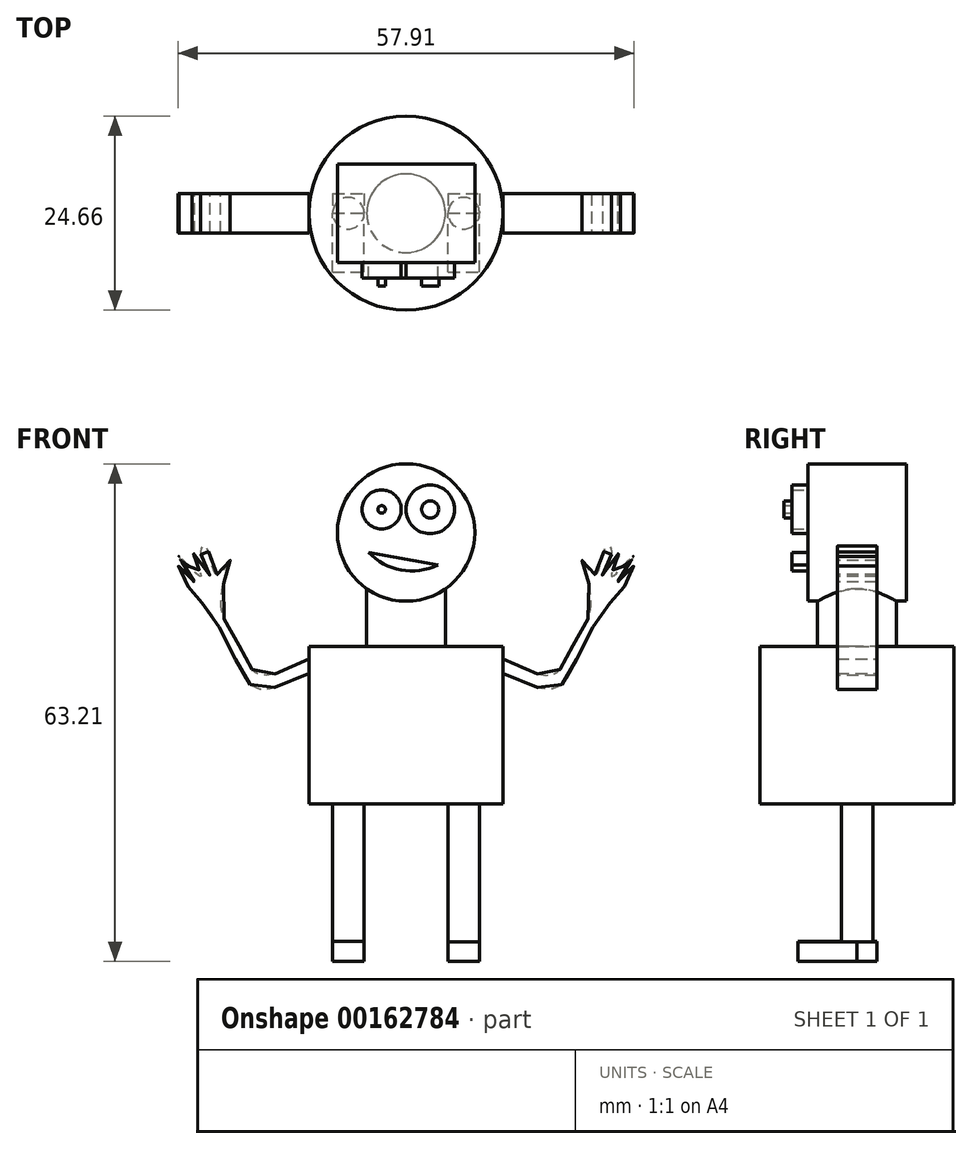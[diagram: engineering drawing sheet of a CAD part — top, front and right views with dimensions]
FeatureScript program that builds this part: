
annotation { "Feature Type Name" : "Feature", "Feature Type Description" : "" }
export const myFeature = defineFeature(function(context is Context, id is Id, definition is map)
    precondition{}
    {
        {
            var Q0;
            Q0=qCreatedBy(makeId("Top.planeOp"),FACE);
            var sketch = newSketch(context, id + "F0", { "sketchPlane" : qUnion([Q0])});
            skCircle(sketch, "E0", {"center": v(-14.66, 0) * mm, "radius": 4 * mm});
            skCircle(sketch, "E1", {"center": v(14.66, 0) * mm, "radius": 4 * mm});
            skSolve(sketch);
        }
        {
            var Q0;
            Q0 = qSketchRegion(id + "F0", true);
            extrude(context, id + "F1", {"entities" : qUnion([Q0]), "depth" : 35 * mm});
        }
        {
            var Q0;
            Q0=makeQuery(id+"F1.opExtrude","CAP_FACE",FACE,{"disambiguationData":[OSD([sQuery(id+"F0.wireOp",EDGE,"E0")])],"isStart":false});
            var sketch = newSketch(context, id + "F2", { "sketchPlane" : qUnion([Q0])});
            skCircle(sketch, "E2.0.0", {"center": v(-14.66, 0) * mm, "radius": 4 * mm});
            skCircle(sketch, "E3.0.0", {"center": v(14.66, 0) * mm, "radius": 4 * mm});
            skCircle(sketch, "E4", {"center": v(0, 0) * mm, "radius": 24.66 * mm});
            skSolve(sketch);
        }
        {
            var Q0;
            Q0=makeQuery(id+"F2.imprint","IMPRINT",FACE,{"disambiguationData":[TD([[makeQuery(id+"F2.imprint","IMPRINT",EDGE,{"derivedFrom":sQuery(id+"F2.wireOp",EDGE,"E2.0.0")}),-1.0]])]});
            var Q1;
            Q1=makeQuery(id+"F2.imprint","IMPRINT",FACE,{"disambiguationData":[TD([[makeQuery(id+"F2.imprint","IMPRINT",EDGE,{"derivedFrom":sQuery(id+"F2.wireOp",EDGE,"E2.0.0")}),1.0]])]});
            var Q2;
            Q2=makeQuery(id+"F2.imprint","IMPRINT",FACE,{"disambiguationData":[TD([[makeQuery(id+"F2.imprint","IMPRINT",EDGE,{"derivedFrom":sQuery(id+"F2.wireOp",EDGE,"E3.0.0")}),1.0]])]});
            extrude(context, id + "F3", {"entities" : qUnion([Q0, Q1, Q2]), "depth" : 40 * mm});
        }
        {
            var Q0;
            Q0=makeQuery(id+"F3.opExtrude","CAP_FACE",FACE,{"disambiguationData":[OSD([sQuery(id+"F2.wireOp",EDGE,"E4")])],"isStart":false});
            var sketch = newSketch(context, id + "F4", { "sketchPlane" : qUnion([Q0])});
            skCircle(sketch, "E5.0", {"center": v(0, 0) * mm, "radius": 24.66 * mm});
            skCircle(sketch, "E6", {"center": v(0, 0) * mm, "radius": 10 * mm});
            skSolve(sketch);
        }
        {
            var Q0;
            Q0=makeQuery(id+"F4.imprint","IMPRINT",FACE,{"disambiguationData":[TD([[makeQuery(id+"F4.imprint","IMPRINT",EDGE,{"derivedFrom":sQuery(id+"F4.wireOp",EDGE,"E6")}),1.0]])]});
            extrude(context, id + "F5", {"entities" : qUnion([Q0]), "operationType" : NewBodyOperationType.ADD, "depth" : 20 * mm});
        }
        {
            var Q0;
            Q0=qCreatedBy(makeId("Front.planeOp"),FACE);
            var sketch = newSketch(context, id + "F6", { "sketchPlane" : qUnion([Q0])});
            skLineSegment(sketch, "E7", {"start": v(-24.66, 35) * mm, "end": v(-24.66, 75) * mm});
            skFitSpline(sketch, "E8", {"points": [v(-24.66, 71.8) * mm, v(-37.62, 67.99) * mm, v(-42.3, 75.12) * mm, v(-47.07, 86.66) * mm, v(-44.74, 96.9) * mm, v(-48.05, 93.32) * mm, v(-50.89, 100.34) * mm, v(-52.23, 99.27) * mm, v(-49.9, 93.2) * mm, v(-54.41, 99.03) * mm, v(-52.18, 92.84) * mm, v(-57.71, 97.95) * mm, v(-53.74, 91.41) * mm, v(-57.72, 95.46) * mm, v(-55.3, 90.1) * mm, v(-51.17, 85.35) * mm, v(-43.7, 72.62) * mm, v(-38.04, 64.42) * mm, v(-24.66, 68.24) * mm], "startDerivative": vector(-210.68, -104.1) * mm, "endDerivative": vector(210.3, 100.49) * mm});
            skFitSpline(sketch, "E9.MirrorCS", {"points": [v(24.66, 71.8) * mm, v(37.62, 67.99) * mm, v(42.3, 75.12) * mm, v(47.07, 86.66) * mm, v(44.74, 96.9) * mm, v(48.05, 93.32) * mm, v(50.89, 100.34) * mm, v(52.23, 99.27) * mm, v(49.9, 93.2) * mm, v(54.41, 99.03) * mm, v(52.18, 92.84) * mm, v(57.71, 97.95) * mm, v(53.74, 91.41) * mm, v(57.72, 95.46) * mm, v(55.3, 90.1) * mm, v(51.17, 85.35) * mm, v(43.7, 72.62) * mm, v(38.04, 64.42) * mm, v(24.66, 68.24) * mm], "startDerivative": vector(210.68, -104.1) * mm, "endDerivative": vector(-210.3, 100.49) * mm});
            skLineSegment(sketch, "E10", {"start": v(24.66, 75) * mm, "end": v(24.66, 35) * mm});
            skSolve(sketch);
        }
        {
            var Q0;
            {var subQ0=sQuery(id+"F6.wireOp",EDGE,"E8");Q0=makeQuery(id+"F6.imprint","IMPRINT",FACE,{"disambiguationData":[TD([[makeQuery(id+"F6.imprint","IMPRINT",EDGE,{"derivedFrom":subQ0}),1.0]])]});}
            var Q1;
            {var subQ0=sQuery(id+"F6.wireOp",EDGE,"E9.MirrorCS");Q1=makeQuery(id+"F6.imprint","IMPRINT",FACE,{"disambiguationData":[TD([[makeQuery(id+"F6.imprint","IMPRINT",EDGE,{"derivedFrom":subQ0}),-1.0]])]});}
            extrude(context, id + "F7", {"entities" : qUnion([Q0, Q1]), "endBound" : BoundingType.SYMMETRIC, "depth" : 10 * mm});
        }
        {
            var Q0;
            Q0=qCreatedBy(makeId("Front.planeOp"),FACE);
            var sketch = newSketch(context, id + "F8", { "sketchPlane" : qUnion([Q0])});
            skLineSegment(sketch, "E11", {"start": v(10, 95) * mm, "end": v(10, 75) * mm});
            skLineSegment(sketch, "E12", {"start": v(-10, 75) * mm, "end": v(-10, 95) * mm});
            skCircle(sketch, "E13", {"center": v(0, 104) * mm, "radius": 17.45 * mm});
            skSolve(sketch);
        }
        {
            var Q0;
            Q0 = qSketchRegion(id + "F8", true);
            extrude(context, id + "F9", {"entities" : qUnion([Q0]), "operationType" : NewBodyOperationType.ADD, "endBound" : BoundingType.SYMMETRIC, "depth" : 25 * mm});
        }
        {
            var Q0;
            Q0=qCreatedBy(makeId("Front.planeOp"),FACE);
            var sketch = newSketch(context, id + "F10", { "sketchPlane" : qUnion([Q0])});
            skLineSegment(sketch, "E14", {"start": v(-18.66, 0.09) * mm, "end": v(-18.66, 35) * mm});
            skLineSegment(sketch, "E15", {"start": v(-10.66, 35) * mm, "end": v(-10.66, 0.09) * mm});
            skLineSegment(sketch, "E16", {"start": v(10.66, 0.04) * mm, "end": v(10.66, 35) * mm});
            skLineSegment(sketch, "E17", {"start": v(18.66, 35) * mm, "end": v(18.66, 0.04) * mm});
            skLineSegment(sketch, "E18.bottom", {"start": v(-18.66, 0.09) * mm, "end": v(-10.66, 0.09) * mm});
            skLineSegment(sketch, "E18.top", {"start": v(-18.66, -4.91) * mm, "end": v(-10.66, -4.91) * mm});
            skLineSegment(sketch, "E18.left", {"start": v(-18.66, 0.09) * mm, "end": v(-18.66, -4.91) * mm});
            skLineSegment(sketch, "E18.right", {"start": v(-10.66, 0.09) * mm, "end": v(-10.66, -4.91) * mm});
            skLineSegment(sketch, "E19.bottom", {"start": v(10.66, 0.04) * mm, "end": v(18.66, 0.04) * mm});
            skLineSegment(sketch, "E19.top", {"start": v(10.66, -4.96) * mm, "end": v(18.66, -4.96) * mm});
            skLineSegment(sketch, "E19.left", {"start": v(10.66, 0.04) * mm, "end": v(10.66, -4.96) * mm});
            skLineSegment(sketch, "E19.right", {"start": v(18.66, 0.04) * mm, "end": v(18.66, -4.96) * mm});
            skSolve(sketch);
        }
        {
            var Q0;
            Q0=makeQuery(id+"F10.imprint","IMPRINT",FACE,{"disambiguationData":[TD([[makeQuery(id+"F10.imprint","IMPRINT",EDGE,{"derivedFrom":sQuery(id+"F10.wireOp",EDGE,"E18.bottom")}),-1.0]])]});
            var Q1;
            Q1=makeQuery(id+"F10.imprint","IMPRINT",FACE,{"disambiguationData":[TD([[makeQuery(id+"F10.imprint","IMPRINT",EDGE,{"derivedFrom":sQuery(id+"F10.wireOp",EDGE,"E19.bottom")}),-1.0]])]});
            extrude(context, id + "F11", {"entities" : qUnion([Q0, Q1]), "depth" : 15 * mm});
        }
        {
            var Q0;
            Q0=makeQuery(id+"F11.opExtrude","CAP_FACE",FACE,{"disambiguationData":[OSD([sQuery(id+"F10.wireOp",EDGE,"E18.bottom"),sQuery(id+"F10.wireOp",EDGE,"E18.top"),sQuery(id+"F10.wireOp",EDGE,"E18.left"),sQuery(id+"F10.wireOp",EDGE,"E18.right")])],"isStart":true});
            var Q1;
            Q1=makeQuery(id+"F11.opExtrude","CAP_FACE",FACE,{"disambiguationData":[OSD([sQuery(id+"F10.wireOp",EDGE,"E19.bottom"),sQuery(id+"F10.wireOp",EDGE,"E19.top"),sQuery(id+"F10.wireOp",EDGE,"E19.left"),sQuery(id+"F10.wireOp",EDGE,"E19.right")])],"isStart":true});
            extrude(context, id + "F12", {"entities" : qUnion([Q0, Q1]), "depth" : 5 * mm});
        }
        {
            var Q0;
            Q0=makeQuery(id+"F7.opExtrude","SWEPT_BODY",BODY,{"disambiguationData":[OSD([sQuery(id+"F6.wireOp",EDGE,"E9.MirrorCS"),sQuery(id+"F6.wireOp",EDGE,"E10")])]});
            var Q1;
            Q1=makeQuery(id+"F7.opExtrude","SWEPT_BODY",BODY,{"disambiguationData":[OSD([sQuery(id+"F6.wireOp",EDGE,"E7"),sQuery(id+"F6.wireOp",EDGE,"E8")])]});
            var Q2;
            Q2=makeQuery(id+"F11.opExtrude","SWEPT_BODY",BODY,{"disambiguationData":[OSD([sQuery(id+"F10.wireOp",EDGE,"E18.bottom"),sQuery(id+"F10.wireOp",EDGE,"E18.top"),sQuery(id+"F10.wireOp",EDGE,"E18.left"),sQuery(id+"F10.wireOp",EDGE,"E18.right")])]});
            var Q3;
            Q3=makeQuery(id+"F3.opExtrude","SWEPT_BODY",BODY,{"disambiguationData":[OSD([sQuery(id+"F2.wireOp",EDGE,"E4")])]});
            var Q4;
            Q4=makeQuery(id+"F1.opExtrude","SWEPT_BODY",BODY,{"disambiguationData":[OSD([sQuery(id+"F0.wireOp",EDGE,"E1")])]});
            var Q5;
            Q5=makeQuery(id+"F11.opExtrude","SWEPT_BODY",BODY,{"disambiguationData":[OSD([sQuery(id+"F10.wireOp",EDGE,"E19.bottom"),sQuery(id+"F10.wireOp",EDGE,"E19.top"),sQuery(id+"F10.wireOp",EDGE,"E19.left"),sQuery(id+"F10.wireOp",EDGE,"E19.right")])]});
            var Q6;
            Q6=makeQuery(id+"F1.opExtrude","SWEPT_BODY",BODY,{"disambiguationData":[OSD([sQuery(id+"F0.wireOp",EDGE,"E0")])]});
            var Q7;
            Q7=makeQuery(id+"F12.opExtrude","SWEPT_BODY",BODY,{"disambiguationData":[OSD([sQuery(id+"F10.wireOp",EDGE,"E19.bottom"),sQuery(id+"F10.wireOp",EDGE,"E19.top"),sQuery(id+"F10.wireOp",EDGE,"E19.left"),sQuery(id+"F10.wireOp",EDGE,"E19.right")])]});
            var Q8;
            Q8=makeQuery(id+"F12.opExtrude","SWEPT_BODY",BODY,{"disambiguationData":[OSD([sQuery(id+"F10.wireOp",EDGE,"E18.bottom"),sQuery(id+"F10.wireOp",EDGE,"E18.top"),sQuery(id+"F10.wireOp",EDGE,"E18.left"),sQuery(id+"F10.wireOp",EDGE,"E18.right")])]});
            var Q9;
            Q9=makeQuery(id+"F11.opExtrude","CAP_VERTEX",VERTEX,{"disambiguationData":[OSD([sQuery(id+"F10.wireOp",EDGE,"E18.bottom"),sQuery(id+"F10.wireOp",EDGE,"E18.left")])],"isStart":false});
            transform(context, id + "F13", {"entities" : qUnion([Q0, Q1, Q2, Q3, Q4, Q5, Q6, Q7, Q8]), "transformType" : TransformType.SCALE_UNIFORMLY, "scale" : 0.5, "scalePoint" : qUnion([Q9]), "makeCopy" : false});
        }
        {
            var Q0;
            Q0=makeQuery(id+"F9.opExtrude","CAP_FACE",FACE,{"disambiguationData":[OSD([sQuery(id+"F8.wireOp",EDGE,"E13")])],"isStart":false});
            var sketch = newSketch(context, id + "F14", { "sketchPlane" : qUnion([Q0])});
            skCircle(sketch, "E20", {"center": v(-12.44, 54.97) * mm, "radius": 2.48 * mm});
            skCircle(sketch, "E21", {"center": v(-6.27, 54.97) * mm, "radius": 3.09 * mm});
            skArc(sketch, "E22", {"start": v(-14.13, 49.53) * mm, "mid": v(-9.98, 47.28) * mm, "end": v(-5.3, 47.9) * mm});
            skLineSegment(sketch, "E23", {"start": v(-14.13, 49.53) * mm, "end": v(-5.3, 47.9) * mm});
            skSolve(sketch);
        }
        {
            var Q0;
            Q0=makeQuery(id+"F14.imprint","IMPRINT",FACE,{"disambiguationData":[TD([[makeQuery(id+"F14.imprint","IMPRINT",EDGE,{"derivedFrom":sQuery(id+"F14.wireOp",EDGE,"E20")}),1.0]])]});
            var Q1;
            Q1=makeQuery(id+"F14.imprint","IMPRINT",FACE,{"disambiguationData":[TD([[makeQuery(id+"F14.imprint","IMPRINT",EDGE,{"derivedFrom":sQuery(id+"F14.wireOp",EDGE,"E21")}),1.0]])]});
            var Q2;
            Q2=makeQuery(id+"F14.imprint","IMPRINT",FACE,{"disambiguationData":[TD([[makeQuery(id+"F14.imprint","IMPRINT",EDGE,{"derivedFrom":sQuery(id+"F14.wireOp",EDGE,"E22")}),1.0]])]});
            extrude(context, id + "F15", {"entities" : qUnion([Q0, Q1, Q2]), "depth" : 2 * mm});
        }
        {
            var Q0;
            Q0=makeQuery(id+"F15.opExtrude","CAP_FACE",FACE,{"disambiguationData":[OSD([sQuery(id+"F14.wireOp",EDGE,"E20")])],"isStart":false});
            var sketch = newSketch(context, id + "F16", { "sketchPlane" : qUnion([Q0])});
            skCircle(sketch, "E24.0", {"center": v(-12.44, 54.97) * mm, "radius": 2.48 * mm});
            skCircle(sketch, "E25.0", {"center": v(-6.27, 54.97) * mm, "radius": 3.09 * mm});
            skCircle(sketch, "E26.0", {"center": v(-12.44, 54.97) * mm, "radius": 0.48 * mm});
            skCircle(sketch, "E27.0", {"center": v(-6.27, 54.97) * mm, "radius": 1.09 * mm});
            skSolve(sketch);
        }
        {
            var Q0;
            Q0=makeQuery(id+"F16.imprint","IMPRINT",FACE,{"disambiguationData":[TD([[makeQuery(id+"F16.imprint","IMPRINT",EDGE,{"derivedFrom":sQuery(id+"F16.wireOp",EDGE,"E26.0")}),1.0]])]});
            var Q1;
            Q1=makeQuery(id+"F16.imprint","IMPRINT",FACE,{"disambiguationData":[TD([[makeQuery(id+"F16.imprint","IMPRINT",EDGE,{"derivedFrom":sQuery(id+"F16.wireOp",EDGE,"E27.0")}),1.0]])]});
            extrude(context, id + "F17", {"entities" : qUnion([Q0, Q1]), "depth" : 1 * mm});
        }
    });
